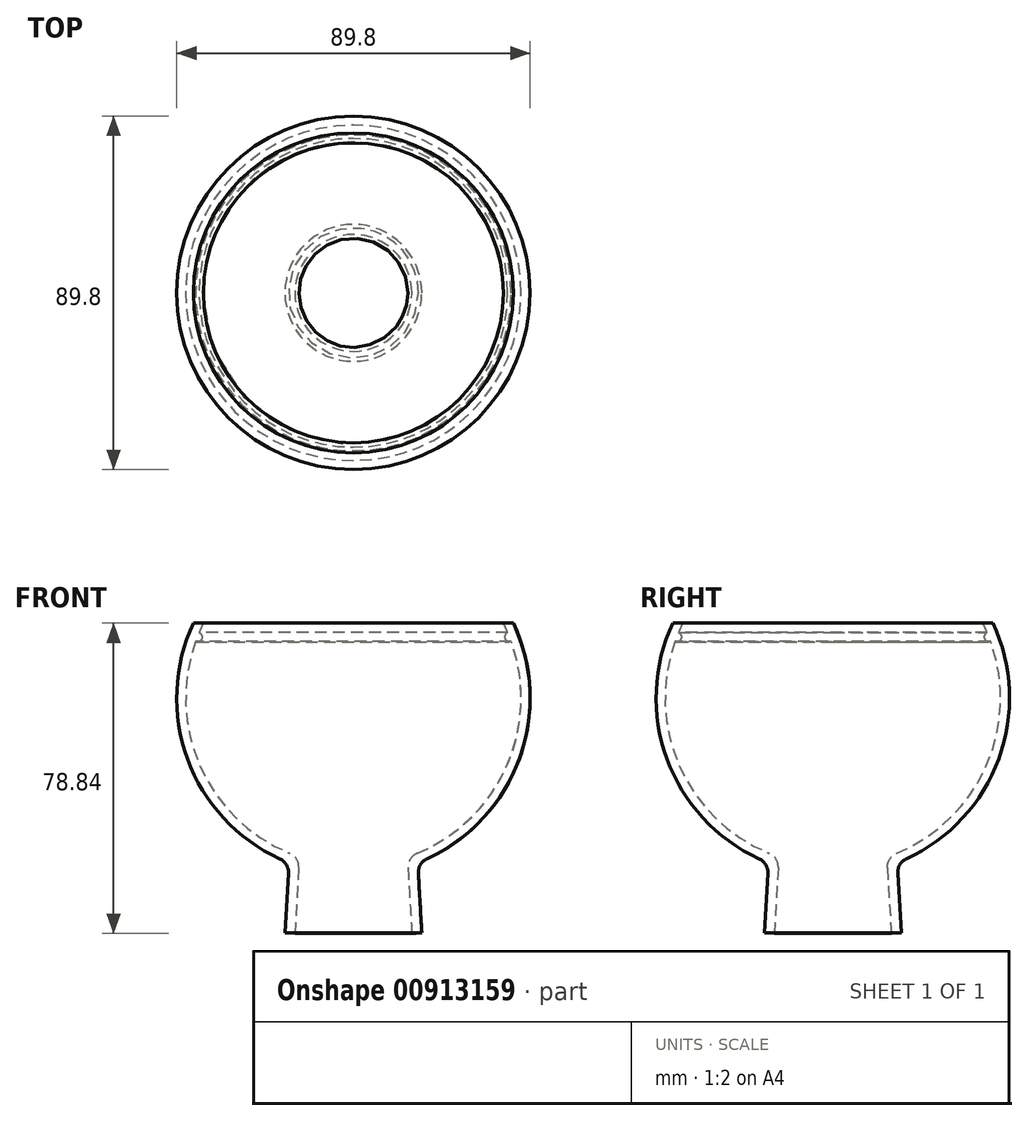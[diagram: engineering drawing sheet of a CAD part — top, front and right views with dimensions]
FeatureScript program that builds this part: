
annotation { "Feature Type Name" : "Feature", "Feature Type Description" : "" }
export const myFeature = defineFeature(function(context is Context, id is Id, definition is map)
    precondition{}
    {
        {
            var Q0;
            Q0=qCreatedBy(makeId("Right.planeOp"),FACE);
            var sketch = newSketch(context, id + "F0", { "sketchPlane" : qUnion([Q0])});
            skLineSegment(sketch, "E0", {"start": v(-2.15, -26.88) * mm, "end": v(-2.15, -26.88) * mm});
            skArc(sketch, "E1", {"start": v(18.7, 29.84) * mm, "mid": v(42.16, 55.21) * mm, "end": v(40.64, 89.73) * mm});
            skLineSegment(sketch, "E2", {"start": v(0, 89.73) * mm, "end": v(0, 0) * mm});
            skArc(sketch, "E3", {"start": v(16.22, 31.25) * mm, "mid": v(39.91, 55.72) * mm, "end": v(38.1, 89.73) * mm});
            skLineSegment(sketch, "E4", {"start": v(16.5, 26.15) * mm, "end": v(17.39, 11.04) * mm});
            skLineSegment(sketch, "E5", {"start": v(17.39, 11.04) * mm, "end": v(14.85, 10.89) * mm});
            skLineSegment(sketch, "E6", {"start": v(14.85, 10.89) * mm, "end": v(13.87, 27.5) * mm});
            skPoint(sketch, "E7.visualSharp", {"position": v(13.7, 30.3) * mm});
            skArc(sketch, "E7.filletArc", {"start": v(16.22, 31.25) * mm, "mid": v(14.45, 29.75) * mm, "end": v(13.87, 27.5) * mm});
            skPoint(sketch, "E8.visualSharp", {"position": v(16.33, 28.83) * mm});
            skArc(sketch, "E8.filletArc", {"start": v(18.7, 29.84) * mm, "mid": v(17.03, 28.34) * mm, "end": v(16.5, 26.15) * mm});
            skLineSegment(sketch, "E9", {"start": v(38.1, 89.73) * mm, "end": v(40.64, 89.73) * mm});
            skArc(sketch, "E10", {"start": v(39.2, 87.34) * mm, "mid": v(38.53, 85.75) * mm, "end": v(40.1, 85.04) * mm});
            skLineSegment(sketch, "E11", {"start": v(0, 10.89) * mm, "end": v(0, 89.73) * mm});
            skSolve(sketch);
        }
        {
            var Q0;
            Q0 = qSketchRegion(id + "F0", true);
            var Q1;
            Q1=sQuery(id+"F0.wireOp",EDGE,"E2");
            revolve(context, id + "F1", {"surfaceOperationType" : NewSurfaceOperationType.NEW, "entities" : qUnion([Q0]), "axis" : qUnion([Q1]), "revolveType" : RevolveType.FULL});
        }
    });
